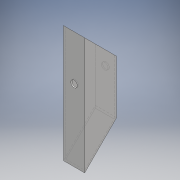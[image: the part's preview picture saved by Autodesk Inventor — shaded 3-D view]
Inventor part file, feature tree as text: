
AUTODESK INVENTOR PART (.ipt)
format: ipt  version: 2018 (Build 220112000, 112)  size: 114,688 bytes
history: native  units: mm
features: extrude x2, sketch x2, other x1, chamfer x1
ambient origin geometry x8: Origin, YZ Plane, XZ Plane, XY Plane, X Axis, Y Axis, Z Axis, Center Point
bodies: Body1 (feature_tree)
feature tree (6):
  other  "ソリッド1"
  extrude  "押し出し1"  Depth=40.0mm
  chamfer  "面取り1"  Distance=60.0mm
  extrude  "押し出し3"  Depth=2.3mm
  sketch  "スケッチ1"
  sketch  "スケッチ5"
